# Revit family: URA SPOT Standard - Permanent_Non Permanent-ENG
name_source: partatom
category: Luminaires
units: mm (PartAtom-declared; Revit-internal decimal feet)

## family parameters
Cote de connecteur circulaire = Utiliser le diamètre
Couper avec des vides une fois chargée = Non
Hôte = Face
Partagée = Non
Repere pour localisation dans la piece = Non
Source d'éclairage = Non
Type d'élément = Normal

## types (5) — shared parameters
Color = White
Connected Object = Non
Connection type = Screw connection
Control system = without
Diameter = 125 mm
Elévation par défaut = 2300 mm
Emergency power supply = Autonomous (individual battery)
Fabricant = LEGRAND
Frequency = 50-60
Function = Escape and mood lighting
General Conditions of Use = https://export.legrand.com
Height = 45 mm
IK = 07
IP = 42
Installation method = Flush-mounting
Material = Plastic
Operating temperature MIN-MAX = -5-35
Pictogram type = other
Power supply = 230 AC/DC
Protection class = II
Recessed height = 42 mm
Standby consumption = 0.0 mA
Switching type = Permanent
URL = https://www.legrand.com
battery status = NiCd
light source = LED not exchangeable
terminal capacity = 1,5-2,5

## per-type parameters (varying)
| type | Autonomy | Product designation | Reference | Spare battery | System power | Useful luminous flux |
| 100LM-1H | 1H | EMERGENCY LIGHT U22ROUND FLUSH PERMANENT - NON PERM 100 LUMENS 1H STANDARD | LG-660042 | 660180 | 3 W | 100 lm |
| 200LM-1H | 1H | EMERGENCY LIGHT U22ROUND FLUSH PERMANENT - NON PERM 200 LUMENS 1H STANDARD | LG-660044 | 660181 | 2 W | 200 lm |
| 350LM-1H | 1H | EMERGENCY LIGHT U22ROUND FLUSH PERMANENT - NON PERM 350 LUMENS 1H STANDARD | LG-660045 | 660184 | 2 W | 350 lm |
| 200LM-2H | 2H | EMERGENCY LIGHT U22ROUND FLUSH PERMANENT - NON PERM 200 LUMENS 2H STANDARD | LG-660047 | 660184 | 2 W | 200 lm |
| 100LM-3H | 3H | EMERGENCY LIGHT U22ROUND FLUSH PERMANENT - NON PERM 100 LUMENS 3H STANDARD | LG-660048 | 660181 | 3 W | 100 lm |
